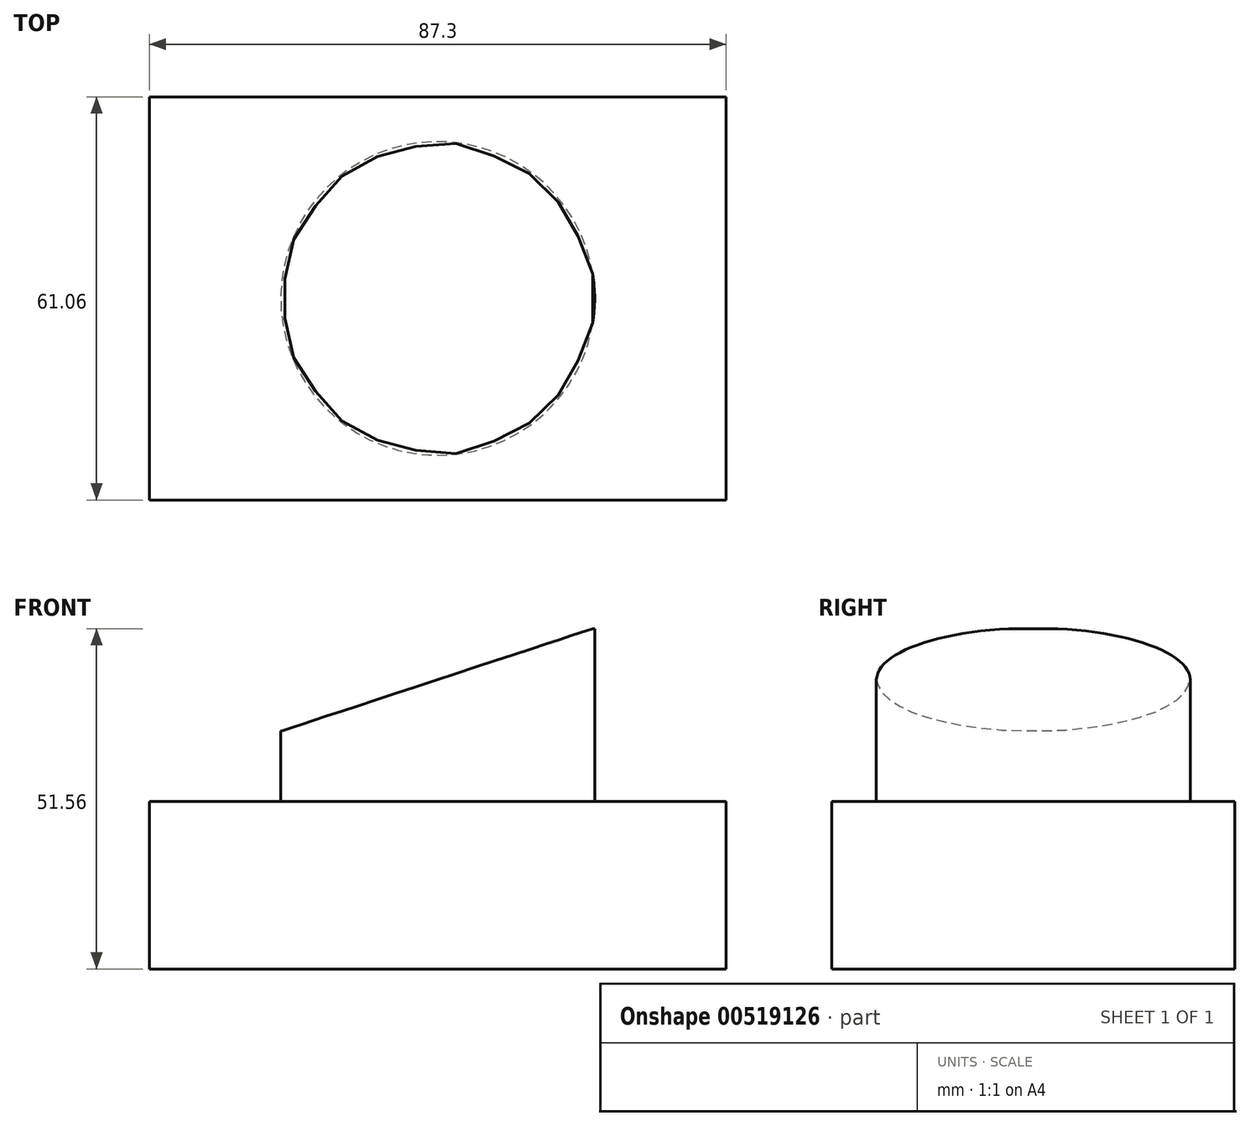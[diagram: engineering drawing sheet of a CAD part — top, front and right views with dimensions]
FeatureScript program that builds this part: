
annotation { "Feature Type Name" : "Feature", "Feature Type Description" : "" }
export const myFeature = defineFeature(function(context is Context, id is Id, definition is map)
    precondition{}
    {
        {
            var Q0;
            Q0=qCreatedBy(makeId("Top.planeOp"),FACE);
            var sketch = newSketch(context, id + "F0", { "sketchPlane" : qUnion([Q0])});
            skLineSegment(sketch, "E0.bottom", {"start": v(43.65, -30.53) * mm, "end": v(-43.65, -30.53) * mm});
            skLineSegment(sketch, "E0.top", {"start": v(43.65, 30.53) * mm, "end": v(-43.65, 30.53) * mm});
            skLineSegment(sketch, "E0.left", {"start": v(43.65, -30.53) * mm, "end": v(43.65, 30.53) * mm});
            skLineSegment(sketch, "E0.right", {"start": v(-43.65, -30.53) * mm, "end": v(-43.65, 30.53) * mm});
            skPoint(sketch, "E0.middle", {"position": v(0, 0) * mm});
            skCircle(sketch, "E1", {"center": v(0, 0) * mm, "radius": 23.76 * mm});
            skSolve(sketch);
        }
        {
            var Q0;
            Q0=makeQuery(id+"F0.imprint","IMPRINT",FACE,{"disambiguationData":[TD([[makeQuery(id+"F0.imprint","IMPRINT",EDGE,{"derivedFrom":sQuery(id+"F0.wireOp",EDGE,"E0.bottom")}),-1.0]])]});
            var Q1;
            Q1=makeQuery(id+"F0.imprint","IMPRINT",FACE,{"disambiguationData":[TD([[makeQuery(id+"F0.imprint","IMPRINT",EDGE,{"derivedFrom":sQuery(id+"F0.wireOp",EDGE,"E1")}),1.0]])]});
            extrude(context, id + "F1", {"entities" : qUnion([Q0, Q1]), "depth" : 25.4 * mm});
        }
        {
            var Q0;
            Q0=makeQuery(id+"F1.opExtrude","CAP_FACE",FACE,{"disambiguationData":[OSD([sQuery(id+"F0.wireOp",EDGE,"E0.bottom"),sQuery(id+"F0.wireOp",EDGE,"E0.top"),sQuery(id+"F0.wireOp",EDGE,"E0.left"),sQuery(id+"F0.wireOp",EDGE,"E0.right")])],"isStart":false});
            var sketch = newSketch(context, id + "F2", { "sketchPlane" : qUnion([Q0])});
            skCircle(sketch, "E2.0", {"center": v(0, 0) * mm, "radius": 23.76 * mm});
            skSolve(sketch);
        }
        {
            var Q0;
            Q0 = qSketchRegion(id + "F2", true);
            extrude(context, id + "F3", {"entities" : qUnion([Q0]), "operationType" : NewBodyOperationType.ADD, "depth" : 26.16 * mm});
        }
        {
            var Q0;
            Q0=makeQuery(id+"F1.opExtrude","SWEPT_FACE",FACE,{"disambiguationData":[OSD([sQuery(id+"F0.wireOp",EDGE,"E0.top")])]});
            var sketch = newSketch(context, id + "F4", { "sketchPlane" : qUnion([Q0])});
            skLineSegment(sketch, "E3", {"start": v(-25.28, 52.16) * mm, "end": v(24.12, 35.9) * mm});
            skLineSegment(sketch, "E4", {"start": v(24.12, 35.9) * mm, "end": v(24.12, 52.16) * mm});
            skLineSegment(sketch, "E5", {"start": v(24.12, 52.16) * mm, "end": v(-25.28, 52.16) * mm});
            skSolve(sketch);
        }
        {
            var Q0;
            Q0 = qSketchRegion(id + "F4", true);
            var Q1;
            Q1=sQuery(id+"F4.wireOp",EDGE,"E5");
            var Q2;
            Q2=makeQuery(id+"F1.opExtrude","SWEPT_FACE",FACE,{"disambiguationData":[OSD([sQuery(id+"F0.wireOp",EDGE,"E0.bottom")])]});
            extrude(context, id + "F5", {"entities" : qUnion([Q0]), "operationType" : NewBodyOperationType.REMOVE, "surfaceEntities" : qUnion([Q1]), "endBound" : BoundingType.UP_TO_SURFACE, "oppositeDirection" : true, "endBoundEntityFace" : qUnion([Q2]), "depth" : 72.39 * mm});
        }
    });
